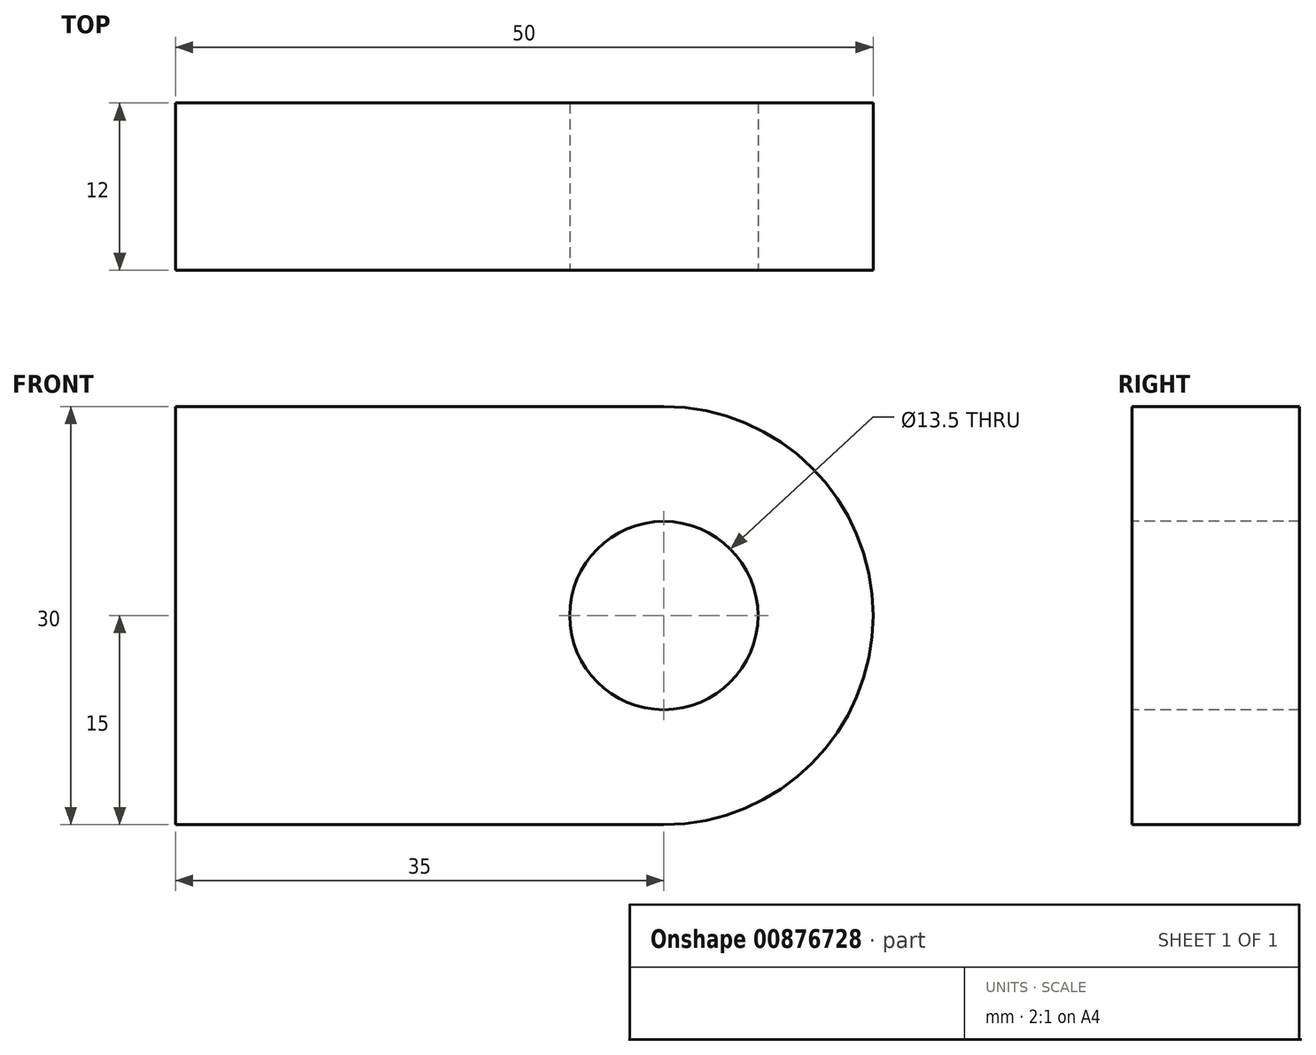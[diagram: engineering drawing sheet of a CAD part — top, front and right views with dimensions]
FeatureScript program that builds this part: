
annotation { "Feature Type Name" : "Feature", "Feature Type Description" : "" }
export const myFeature = defineFeature(function(context is Context, id is Id, definition is map)
    precondition{}
    {
        {
            var Q0;
            Q0=qCreatedBy(makeId("Front.planeOp"),FACE);
            var sketch = newSketch(context, id + "F0", { "sketchPlane" : qUnion([Q0])});
            skLineSegment(sketch, "E0.bottom", {"start": v(0, 0) * mm, "end": v(35, 0) * mm});
            skLineSegment(sketch, "E0.top", {"start": v(0, 30) * mm, "end": v(35, 30) * mm});
            skLineSegment(sketch, "E0.left", {"start": v(0, 0) * mm, "end": v(0, 30) * mm});
            skLineSegment(sketch, "E0.right", {"start": v(50, 15) * mm, "end": v(50, 15) * mm});
            skPoint(sketch, "E1.visualSharp", {"position": v(50, 30) * mm});
            skArc(sketch, "E1.filletArc", {"start": v(50, 15) * mm, "mid": v(45.6, 25.6) * mm, "end": v(35, 30) * mm});
            skPoint(sketch, "E2.visualSharp", {"position": v(50, 0) * mm});
            skArc(sketch, "E2.filletArc", {"start": v(35, 0) * mm, "mid": v(45.6, 4.4) * mm, "end": v(50, 15) * mm});
            skSolve(sketch);
        }
        {
            var Q0;
            Q0=makeQuery(id+"F0.imprint","IMPRINT",FACE,{"disambiguationData":[TD([[makeQuery(id+"F0.imprint","IMPRINT",EDGE,{"derivedFrom":sQuery(id+"F0.wireOp",EDGE,"E0.bottom")}),1.0]])]});
            extrude(context, id + "F1", {"entities" : qUnion([Q0]), "depth" : 12 * mm, "offsetDistance" : 25 * mm});
        }
        {
            var Q0;
            Q0=makeQuery(id+"F1.opExtrude","CAP_FACE",FACE,{"disambiguationData":[OSD([sQuery(id+"F0.wireOp",EDGE,"E0.bottom"),sQuery(id+"F0.wireOp",EDGE,"E0.top"),sQuery(id+"F0.wireOp",EDGE,"E0.left"),sQuery(id+"F0.wireOp",EDGE,"E1.filletArc"),sQuery(id+"F0.wireOp",EDGE,"E2.filletArc")])],"isStart":false});
            var sketch = newSketch(context, id + "F2", { "sketchPlane" : qUnion([Q0])});
            skPoint(sketch, "E3", {"position": v(35, 15) * mm});
            skSolve(sketch);
        }
        {
            var Q0;
            Q0=sQuery(id+"F2.wireOp",VERTEX,"E3");
            var Q1;
            Q1=makeQuery(id+"F1.opExtrude","SWEPT_BODY",BODY,{"disambiguationData":[OSD([sQuery(id+"F0.wireOp",EDGE,"E0.bottom"),sQuery(id+"F0.wireOp",EDGE,"E0.top"),sQuery(id+"F0.wireOp",EDGE,"E0.left"),sQuery(id+"F0.wireOp",EDGE,"E1.filletArc"),sQuery(id+"F0.wireOp",EDGE,"E2.filletArc")])]});
            hole(context, id + "F3", {"style" : HoleStyle.SIMPLE, "endStyle" : HoleEndStyle.THROUGH, "standardTappedOrClearance" : lookupTablePath({ "fit" : "Normal", "standard" : "ISO", "size" : "M12", "type" : "Clearance" }), "standardBlindInLast" : lookupTablePath({ "fit" : "Normal", "standard" : "ISO", "size" : "M12", "type" : "Clearance" }), "holeDiameter" : 13.5 * mm, "majorDiameter" : 5 * mm, "isTappedThrough" : true, "tappedDepth" : 12 * mm, "tapClearance" : 3, "locations" : qUnion([Q0]), "scope" : qUnion([Q1])});
        }
    });
